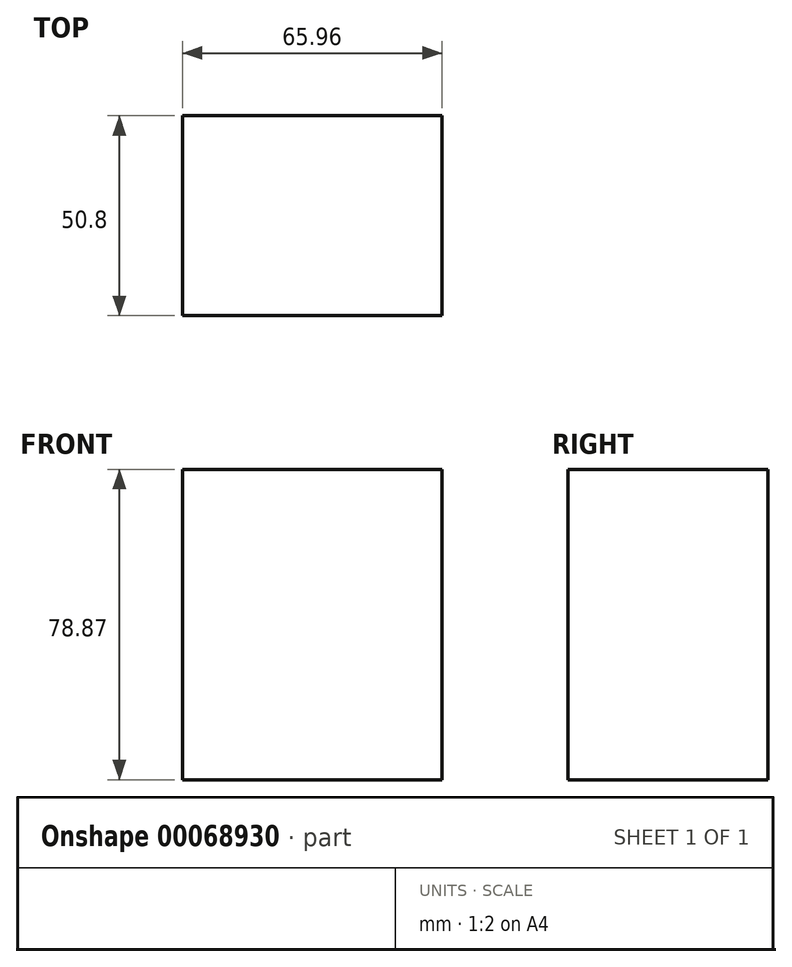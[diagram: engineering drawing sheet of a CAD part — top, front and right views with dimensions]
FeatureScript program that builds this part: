
annotation { "Feature Type Name" : "Feature", "Feature Type Description" : "" }
export const myFeature = defineFeature(function(context is Context, id is Id, definition is map)
    precondition{}
    {
        {
            var Q0;
            Q0=qCreatedBy(makeId("Front.planeOp"),FACE);
            var sketch = newSketch(context, id + "F0", { "sketchPlane" : qUnion([Q0])});
            skLineSegment(sketch, "E0", {"start": v(-125.62, 41.19) * mm, "end": v(-125.62, -47.28) * mm});
            skLineSegment(sketch, "E1", {"start": v(-125.62, -47.28) * mm, "end": v(-59.66, -47.28) * mm});
            skLineSegment(sketch, "E2", {"start": v(-59.66, -47.28) * mm, "end": v(-59.66, 31.59) * mm});
            skLineSegment(sketch, "E3", {"start": v(-59.66, 31.59) * mm, "end": v(-125.62, 31.59) * mm});
            skSolve(sketch);
        }
        {
            var Q0;
            Q0 = qSketchRegion(id + "F0", true);
            extrude(context, id + "F1", {"entities" : qUnion([Q0]), "depth" : 50.8 * mm});
        }
    });
